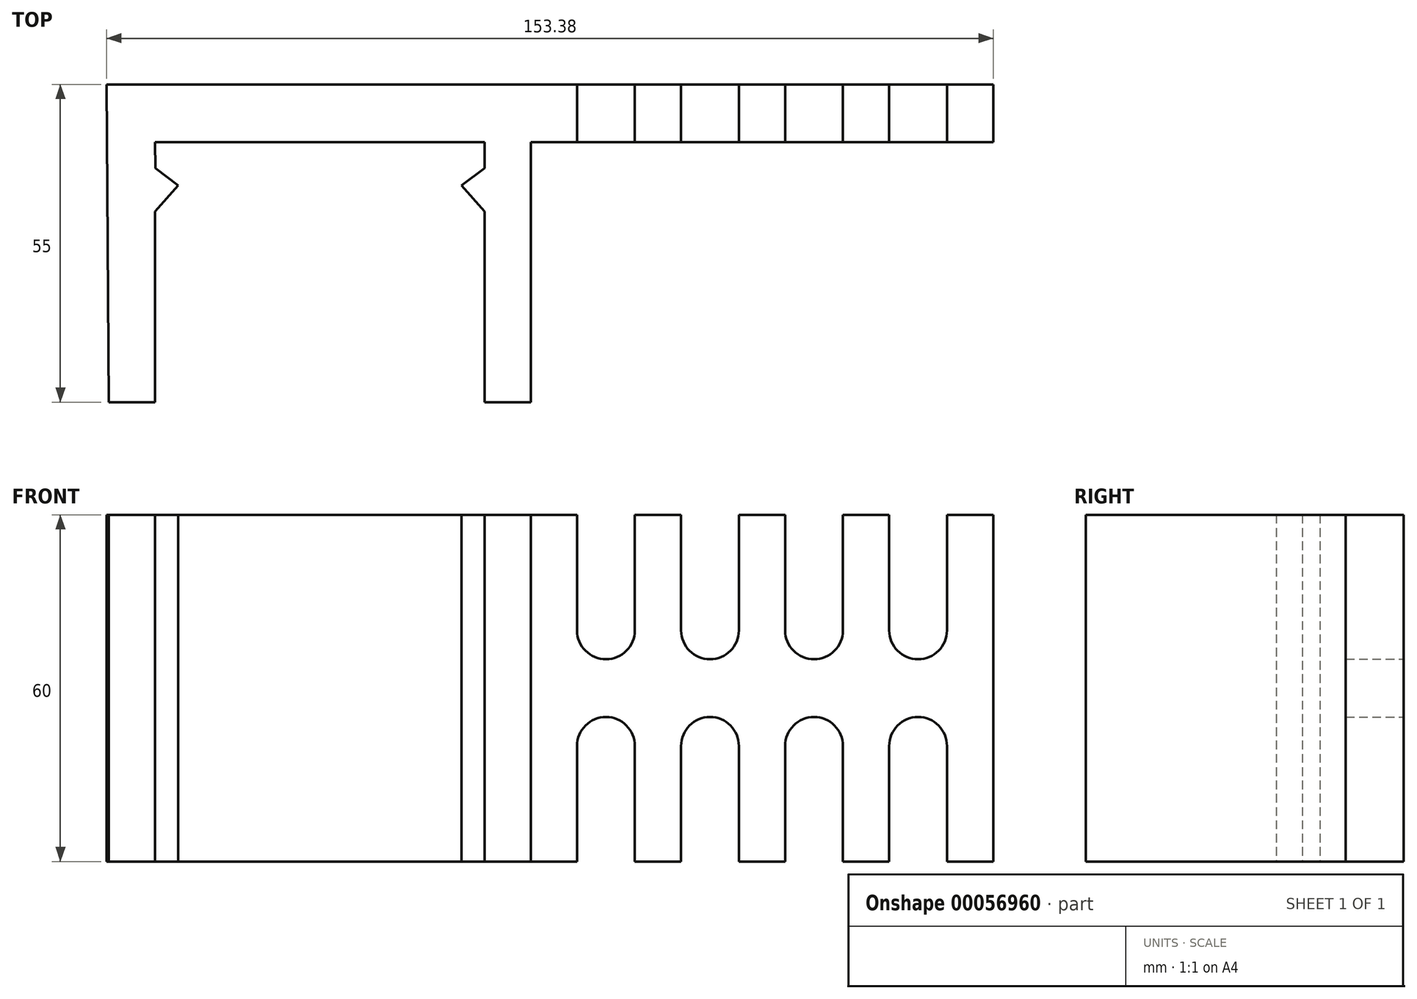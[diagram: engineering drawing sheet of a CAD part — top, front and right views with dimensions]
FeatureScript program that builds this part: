
annotation { "Feature Type Name" : "Feature", "Feature Type Description" : "" }
export const myFeature = defineFeature(function(context is Context, id is Id, definition is map)
    precondition{}
    {
        {
            var Q0;
            Q0=qCreatedBy(makeId("Top.planeOp"),FACE);
            var sketch = newSketch(context, id + "F0", { "sketchPlane" : qUnion([Q0])});
            skLineSegment(sketch, "E0", {"start": v(-19.42, -22.66) * mm, "end": v(-11.42, -22.66) * mm});
            skLineSegment(sketch, "E1", {"start": v(-11.42, 22.34) * mm, "end": v(45.58, 22.34) * mm});
            skLineSegment(sketch, "E2", {"start": v(45.58, 22.34) * mm, "end": v(45.58, 17.84) * mm});
            skLineSegment(sketch, "E3", {"start": v(45.58, 17.84) * mm, "end": v(41.58, 14.84) * mm});
            skLineSegment(sketch, "E4", {"start": v(45.58, 10.34) * mm, "end": v(45.58, -22.66) * mm});
            skLineSegment(sketch, "E5", {"start": v(45.58, -22.66) * mm, "end": v(53.58, -22.66) * mm});
            skLineSegment(sketch, "E6", {"start": v(53.58, -22.66) * mm, "end": v(53.58, 22.34) * mm});
            skLineSegment(sketch, "E7", {"start": v(53.58, 22.34) * mm, "end": v(133.58, 22.34) * mm});
            skLineSegment(sketch, "E8", {"start": v(133.58, 22.34) * mm, "end": v(133.58, 32.34) * mm});
            skLineSegment(sketch, "E9", {"start": v(133.58, 32.34) * mm, "end": v(-19.8, 32.34) * mm});
            skLineSegment(sketch, "E10", {"start": v(-19.8, 32.34) * mm, "end": v(-19.42, -22.66) * mm});
            skLineSegment(sketch, "E11", {"start": v(-11.42, 22.34) * mm, "end": v(-11.4, 17.84) * mm});
            skLineSegment(sketch, "E12", {"start": v(-11.4, 17.84) * mm, "end": v(-7.42, 14.84) * mm});
            skLineSegment(sketch, "E13", {"start": v(-11.42, 10.34) * mm, "end": v(-7.42, 14.84) * mm});
            skLineSegment(sketch, "E14", {"start": v(-11.42, -22.66) * mm, "end": v(-11.42, 10.34) * mm});
            skLineSegment(sketch, "E15", {"start": v(45.58, 10.34) * mm, "end": v(41.58, 14.84) * mm});
            skSolve(sketch);
        }
        {
            var Q0;
            Q0=makeQuery(id+"F0.imprint","IMPRINT",FACE,{"disambiguationData":[TD([[makeQuery(id+"F0.imprint","IMPRINT",EDGE,{"derivedFrom":sQuery(id+"F0.wireOp",EDGE,"E0")}),1.0]])]});
            extrude(context, id + "F1", {"entities" : qUnion([Q0]), "depth" : 60 * mm});
        }
        {
            var Q0;
            Q0=makeQuery(id+"F1.opExtrude","SWEPT_FACE",FACE,{"disambiguationData":[OSD([sQuery(id+"F0.wireOp",EDGE,"E9")])]});
            var sketch = newSketch(context, id + "F2", { "sketchPlane" : qUnion([Q0])});
            skLineSegment(sketch, "E16", {"start": v(-125.58, 60) * mm, "end": v(-125.58, 40) * mm});
            skLineSegment(sketch, "E17", {"start": v(-115.58, 60) * mm, "end": v(-115.58, 40) * mm});
            skLineSegment(sketch, "E18", {"start": v(-133.58, 30) * mm, "end": v(19.8, 30) * mm, "construction": true});
            skLineSegment(sketch, "E19", {"start": v(-107.58, 60) * mm, "end": v(-107.58, 40) * mm});
            skLineSegment(sketch, "E20", {"start": v(-97.58, 60) * mm, "end": v(-97.58, 40) * mm});
            skLineSegment(sketch, "E21", {"start": v(-89.58, 60) * mm, "end": v(-89.58, 40) * mm});
            skLineSegment(sketch, "E22", {"start": v(-79.58, 60) * mm, "end": v(-79.58, 40) * mm});
            skLineSegment(sketch, "E23", {"start": v(-71.58, 60) * mm, "end": v(-71.58, 40) * mm});
            skLineSegment(sketch, "E24", {"start": v(-125.58, 60) * mm, "end": v(-115.58, 60) * mm});
            skArc(sketch, "E25", {"start": v(-125.58, 40) * mm, "mid": v(-120.58, 35) * mm, "end": v(-115.58, 40) * mm});
            skArc(sketch, "E26", {"start": v(-107.58, 40) * mm, "mid": v(-102.58, 35) * mm, "end": v(-97.58, 40) * mm});
            skArc(sketch, "E27", {"start": v(-89.58, 40) * mm, "mid": v(-84.58, 35) * mm, "end": v(-79.58, 40) * mm});
            skLineSegment(sketch, "E28", {"start": v(-61.58, 60) * mm, "end": v(-61.58, 40) * mm});
            skArc(sketch, "E29", {"start": v(-71.58, 40) * mm, "mid": v(-66.58, 35) * mm, "end": v(-61.58, 40) * mm});
            skLineSegment(sketch, "E30", {"start": v(-107.58, 60) * mm, "end": v(-97.58, 60) * mm});
            skLineSegment(sketch, "E31", {"start": v(-89.58, 60) * mm, "end": v(-79.58, 60) * mm});
            skLineSegment(sketch, "E32", {"start": v(-71.58, 60) * mm, "end": v(-61.58, 60) * mm});
            skLineSegment(sketch, "E33.MirrorCS", {"start": v(-79.58, 0) * mm, "end": v(-79.58, 20) * mm});
            skLineSegment(sketch, "E34.MirrorCS", {"start": v(-71.58, 0) * mm, "end": v(-71.58, 20) * mm});
            skLineSegment(sketch, "E35.MirrorCS", {"start": v(-89.58, 0) * mm, "end": v(-89.58, 20) * mm});
            skLineSegment(sketch, "E36.MirrorCS", {"start": v(-97.58, 0) * mm, "end": v(-97.58, 20) * mm});
            skLineSegment(sketch, "E37.MirrorCS", {"start": v(-125.58, 0) * mm, "end": v(-115.58, 0) * mm});
            skArc(sketch, "E38.MirrorCS", {"start": v(-125.58, 20) * mm, "mid": v(-120.58, 25) * mm, "end": v(-115.58, 20) * mm});
            skArc(sketch, "E39.MirrorCS", {"start": v(-107.58, 20) * mm, "mid": v(-102.58, 25) * mm, "end": v(-97.58, 20) * mm});
            skLineSegment(sketch, "E40.MirrorCS", {"start": v(-107.58, 0) * mm, "end": v(-107.58, 20) * mm});
            skArc(sketch, "E41.MirrorCS", {"start": v(-89.58, 20) * mm, "mid": v(-84.58, 25) * mm, "end": v(-79.58, 20) * mm});
            skLineSegment(sketch, "E42.MirrorCS", {"start": v(-61.58, 0) * mm, "end": v(-61.58, 20) * mm});
            skLineSegment(sketch, "E43.MirrorCS", {"start": v(-115.58, 0) * mm, "end": v(-115.58, 20) * mm});
            skLineSegment(sketch, "E44.MirrorCS", {"start": v(-125.58, 0) * mm, "end": v(-125.58, 20) * mm});
            skLineSegment(sketch, "E45.MirrorCS", {"start": v(-89.58, 0) * mm, "end": v(-79.58, 0) * mm});
            skLineSegment(sketch, "E46.MirrorCS", {"start": v(-71.58, 0) * mm, "end": v(-61.58, 0) * mm});
            skLineSegment(sketch, "E47.MirrorCS", {"start": v(-107.58, 0) * mm, "end": v(-97.58, 0) * mm});
            skArc(sketch, "E48.MirrorCS", {"start": v(-71.58, 20) * mm, "mid": v(-66.58, 25) * mm, "end": v(-61.58, 20) * mm});
            skSolve(sketch);
        }
        {
            var Q0;
            Q0 = qSketchRegion(id + "F2", true);
            extrude(context, id + "F3", {"entities" : qUnion([Q0]), "operationType" : NewBodyOperationType.REMOVE, "oppositeDirection" : true, "depth" : 11 * mm});
        }
    });
